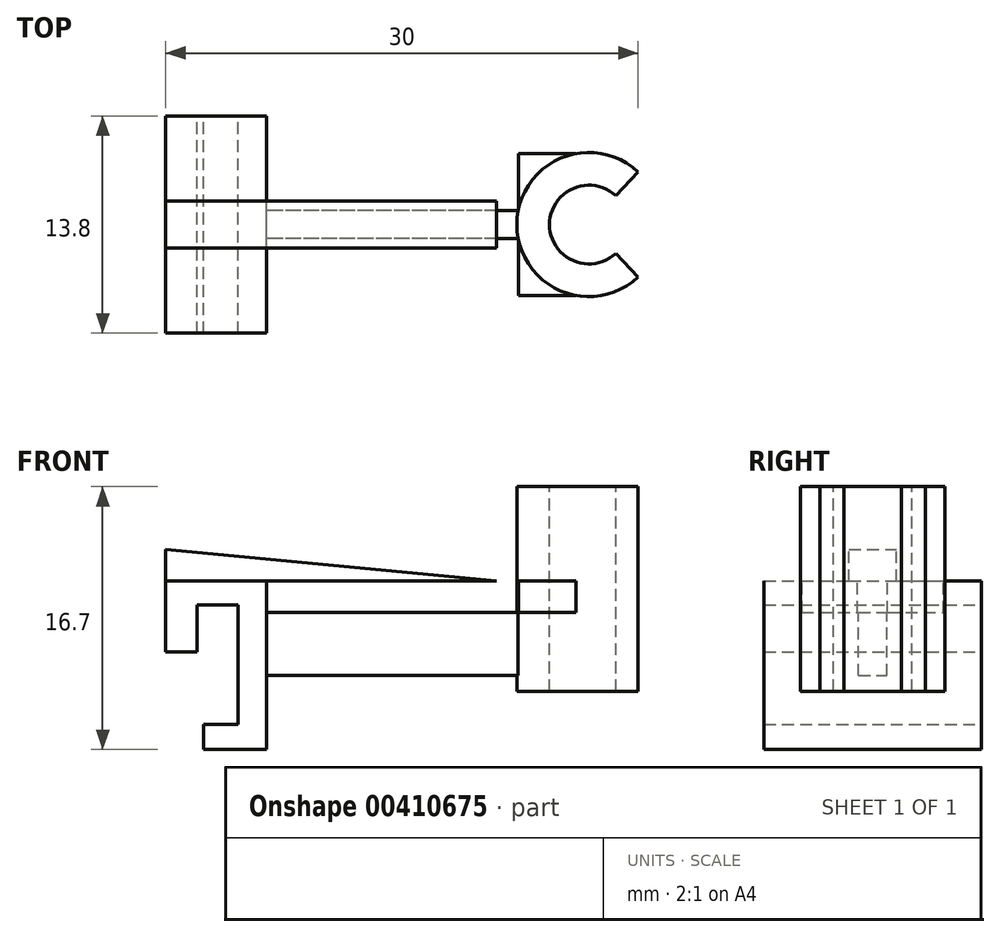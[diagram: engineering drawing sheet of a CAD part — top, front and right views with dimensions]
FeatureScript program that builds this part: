
annotation { "Feature Type Name" : "Feature", "Feature Type Description" : "" }
export const myFeature = defineFeature(function(context is Context, id is Id, definition is map)
    precondition{}
    {
        {
            var Q0;
            Q0=qCreatedBy(makeId("Front.planeOp"),FACE);
            var sketch = newSketch(context, id + "F0", { "sketchPlane" : qUnion([Q0])});
            skLineSegment(sketch, "E0.bottom", {"start": v(8, -2) * mm, "end": v(-8, -2) * mm});
            skLineSegment(sketch, "E0.top", {"start": v(8, 2) * mm, "end": v(-8, 2) * mm});
            skLineSegment(sketch, "E0.left", {"start": v(8, -2) * mm, "end": v(8, 2) * mm});
            skLineSegment(sketch, "E0.right", {"start": v(-8, -2) * mm, "end": v(-8, 2) * mm});
            skPoint(sketch, "E0.middle", {"position": v(0, 0) * mm});
            skLineSegment(sketch, "E1.bottom", {"start": v(8, -3) * mm, "end": v(15.6, -3) * mm});
            skLineSegment(sketch, "E1.top", {"start": v(8, 10) * mm, "end": v(15.6, 10) * mm});
            skLineSegment(sketch, "E1.left", {"start": v(8, -3) * mm, "end": v(8, 10) * mm});
            skLineSegment(sketch, "E2.bottom", {"start": v(12, 2) * mm, "end": v(-8, 2) * mm});
            skLineSegment(sketch, "E2.top", {"start": v(12, 4) * mm, "end": v(-8, 4) * mm});
            skLineSegment(sketch, "E2.left", {"start": v(12, 2) * mm, "end": v(12, 4) * mm});
            skLineSegment(sketch, "E2.right", {"start": v(-8, 2) * mm, "end": v(-8, 4) * mm});
            skLineSegment(sketch, "E3", {"start": v(-8, 4) * mm, "end": v(-8, -6.7) * mm});
            skLineSegment(sketch, "E4", {"start": v(-8, -6.7) * mm, "end": v(-12, -6.7) * mm});
            skLineSegment(sketch, "E5", {"start": v(-12, -6.7) * mm, "end": v(-12, -5.1) * mm});
            skLineSegment(sketch, "E6", {"start": v(-12, -5.1) * mm, "end": v(-9.8, -5.1) * mm});
            skLineSegment(sketch, "E7", {"start": v(-9.8, -5.1) * mm, "end": v(-9.8, 2.5) * mm});
            skLineSegment(sketch, "E8", {"start": v(-9.8, 2.5) * mm, "end": v(-12.4, 2.5) * mm});
            skLineSegment(sketch, "E9", {"start": v(-12.4, 2.5) * mm, "end": v(-12.4, -0.5) * mm});
            skLineSegment(sketch, "E10", {"start": v(-12.4, -0.5) * mm, "end": v(-14.4, -0.5) * mm});
            skLineSegment(sketch, "E11", {"start": v(-14.4, -0.5) * mm, "end": v(-14.4, 4) * mm});
            skLineSegment(sketch, "E12", {"start": v(-14.4, 4) * mm, "end": v(-8, 4) * mm});
            skLineSegment(sketch, "E13", {"start": v(-14.4, 4) * mm, "end": v(-14.4, 6) * mm});
            skLineSegment(sketch, "E14", {"start": v(-14.4, 6) * mm, "end": v(6.6, 4) * mm});
            skLineSegment(sketch, "E15", {"start": v(6.6, 4) * mm, "end": v(-14.4, 4) * mm});
            skLineSegment(sketch, "E16.bottom", {"start": v(8, 10) * mm, "end": v(12.5, 10) * mm});
            skLineSegment(sketch, "E16.top", {"start": v(8, -3) * mm, "end": v(12.5, -3) * mm});
            skLineSegment(sketch, "E16.left", {"start": v(8, 10) * mm, "end": v(8, -3) * mm});
            skLineSegment(sketch, "E16.right", {"start": v(12.5, 10) * mm, "end": v(12.5, -3) * mm});
            skLineSegment(sketch, "E17.bottom", {"start": v(8, 10) * mm, "end": v(17, 10) * mm});
            skLineSegment(sketch, "E17.top", {"start": v(8, -3) * mm, "end": v(17, -3) * mm});
            skLineSegment(sketch, "E17.right", {"start": v(17, 10) * mm, "end": v(17, -3) * mm});
            skSolve(sketch);
        }
        {
            var Q0;
            {var subQ5=sQuery(id+"F0.wireOp",EDGE,"E4");Q0=makeQuery(id+"F0.imprint","IMPRINT",FACE,{"disambiguationData":[TD([[makeQuery(id+"F0.imprint","IMPRINT",EDGE,{"derivedFrom":subQ5}),-1.0]])]});}
            extrude(context, id + "F1", {"entities" : qUnion([Q0]), "endBound" : BoundingType.SYMMETRIC, "depth" : 13.8 * mm});
        }
        {
            var Q0;
            {var subQ0=sQuery(id+"F0.wireOp",EDGE,"E0.bottom");Q0=makeQuery(id+"F0.imprint","IMPRINT",FACE,{"disambiguationData":[TD([[makeQuery(id+"F0.imprint","IMPRINT",EDGE,{"derivedFrom":subQ0}),-1.0]])]});}
            extrude(context, id + "F2", {"entities" : qUnion([Q0]), "operationType" : NewBodyOperationType.ADD, "endBound" : BoundingType.SYMMETRIC, "depth" : 1.8 * mm});
        }
        {
            var Q0;
            {var subQ0=sQuery(id+"F0.wireOp",EDGE,"E2.left");Q0=makeQuery(id+"F0.imprint","IMPRINT",FACE,{"disambiguationData":[TD([[makeQuery(id+"F0.imprint","IMPRINT",EDGE,{"derivedFrom":subQ0}),1.0]])]});}
            var Q1;
            {var subQ0=sQuery(id+"F0.wireOp",EDGE,"E3");var subQ1=sQuery(id+"F0.wireOp",EDGE,"E2.bottom");var subQ2=makeQuery(id+"F0.imprint","INTERSECT",VERTEX,{"derivedFrom":[subQ1,subQ0]});Q1=makeQuery(id+"F0.imprint","IMPRINT",FACE,{"disambiguationData":[TD([[makeQuery(id+"F0.imprint","IMPRINT",EDGE,{"disambiguationData":[TD([[subQ2,1.0]])],"derivedFrom":subQ1}),-1.0]])]});}
            extrude(context, id + "F3", {"entities" : qUnion([Q0, Q1]), "operationType" : NewBodyOperationType.ADD, "endBound" : BoundingType.SYMMETRIC, "depth" : 9 * mm});
        }
        {
            var Q0;
            {var subQ0=sQuery(id+"F0.wireOp",EDGE,"E13");Q0=makeQuery(id+"F0.imprint","IMPRINT",FACE,{"disambiguationData":[TD([[makeQuery(id+"F0.imprint","IMPRINT",EDGE,{"derivedFrom":subQ0}),-1.0]])]});}
            extrude(context, id + "F4", {"entities" : qUnion([Q0]), "operationType" : NewBodyOperationType.ADD, "endBound" : BoundingType.SYMMETRIC, "depth" : 3 * mm});
        }
        {
            var Q0;
            Q0=qCreatedBy(makeId("Top.planeOp"),FACE);
            var sketch = newSketch(context, id + "F5", { "sketchPlane" : qUnion([Q0])});
            skCircle(sketch, "E18", {"center": v(12.47, 0) * mm, "radius": 4.58 * mm});
            skLineSegment(sketch, "E19", {"start": v(15.6, 0) * mm, "end": v(15.6, -3.34) * mm});
            skLineSegment(sketch, "E20", {"start": v(15.6, 0) * mm, "end": v(15.6, 3.34) * mm});
            skLineSegment(sketch, "E21", {"start": v(15.6, 3.34) * mm, "end": v(12.47, 0) * mm});
            skLineSegment(sketch, "E22", {"start": v(15.6, -3.34) * mm, "end": v(12.47, 0) * mm});
            skSolve(sketch);
        }
        {
            var Q0;
            Q0=makeQuery(id+"F5.imprint","IMPRINT",FACE,{"disambiguationData":[TD([[makeQuery(id+"F5.imprint","IMPRINT",EDGE,{"derivedFrom":sQuery(id+"F5.wireOp",EDGE,"E18")}),1.0]])]});
            var Q1;
            Q1=sQuery(id+"F5.wireOp",EDGE,"E18");
            extrude(context, id + "F6", {"entities" : qUnion([Q0]), "operationType" : NewBodyOperationType.ADD, "surfaceEntities" : qUnion([Q1]), "oppositeDirection" : true, "depth" : 3 * mm, "hasSecondDirection" : true, "secondDirectionOppositeDirection" : false, "secondDirectionDepth" : 10 * mm});
        }
        {
            var Q0;
            Q0=sQuery(id+"F5.wireOp",VERTEX,"E18.center");
            var Q1;
            Q1=makeQuery(id+"F1.opExtrude","SWEPT_BODY",BODY,{"disambiguationData":[OSD([sQuery(id+"F0.wireOp",EDGE,"E3"),sQuery(id+"F0.wireOp",EDGE,"E4"),sQuery(id+"F0.wireOp",EDGE,"E5"),sQuery(id+"F0.wireOp",EDGE,"E6"),sQuery(id+"F0.wireOp",EDGE,"E7"),sQuery(id+"F0.wireOp",EDGE,"E8"),sQuery(id+"F0.wireOp",EDGE,"E9"),sQuery(id+"F0.wireOp",EDGE,"E10"),sQuery(id+"F0.wireOp",EDGE,"E11"),sQuery(id+"F0.wireOp",EDGE,"E15")])]});
            hole(context, id + "F7", {"style" : HoleStyle.SIMPLE, "endStyle" : HoleEndStyle.THROUGH, "holeDiameter" : 5 * mm, "isTappedThrough" : true, "tappedDepth" : 12 * mm, "tapClearance" : 3, "locations" : qUnion([Q0]), "scope" : qUnion([Q1])});
        }
        {
            var Q0;
            Q0=sQuery(id+"F5.wireOp",VERTEX,"E18.center");
            var Q1;
            Q1=makeQuery(id+"F1.opExtrude","SWEPT_BODY",BODY,{"disambiguationData":[OSD([sQuery(id+"F0.wireOp",EDGE,"E3"),sQuery(id+"F0.wireOp",EDGE,"E4"),sQuery(id+"F0.wireOp",EDGE,"E5"),sQuery(id+"F0.wireOp",EDGE,"E6"),sQuery(id+"F0.wireOp",EDGE,"E7"),sQuery(id+"F0.wireOp",EDGE,"E8"),sQuery(id+"F0.wireOp",EDGE,"E9"),sQuery(id+"F0.wireOp",EDGE,"E10"),sQuery(id+"F0.wireOp",EDGE,"E11"),sQuery(id+"F0.wireOp",EDGE,"E15")])]});
            hole(context, id + "F8", {"style" : HoleStyle.SIMPLE, "endStyle" : HoleEndStyle.THROUGH, "oppositeDirection" : true, "holeDiameter" : 5 * mm, "isTappedThrough" : true, "tappedDepth" : 12 * mm, "tapClearance" : 3, "locations" : qUnion([Q0]), "scope" : qUnion([Q1])});
        }
        {
            var Q0;
            Q0=makeQuery(id+"F6.opExtrude","CAP_FACE",FACE,{"disambiguationData":[OSD([sQuery(id+"F5.wireOp",EDGE,"E18"),sQuery(id+"F5.wireOp",EDGE,"E19"),sQuery(id+"F5.wireOp",EDGE,"E20")])],"isStart":true});
            extrude(context, id + "F9", {"entities" : qUnion([Q0]), "operationType" : NewBodyOperationType.REMOVE, "oppositeDirection" : true, "depth" : 25 * mm});
        }
    });
